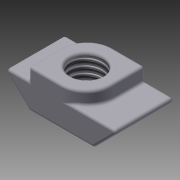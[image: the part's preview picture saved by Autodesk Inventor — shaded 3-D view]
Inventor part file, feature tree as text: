
AUTODESK INVENTOR PART (.ipt)
format: ipt  version: 2011 (Build 150239000, 239)  size: 196,608 bytes
history: native  units: in
note: dims shown in document units (in); Inventor stores cm internally (conversion verified against a paired STEP export)
features: extrude x2, fillet x2, sketch x2, thread x1
ambient origin geometry x8: Origin, YZ Plane, XZ Plane, XY Plane, X Axis, Y Axis, Z Axis, Center Point
bodies: Solid1 (feature_tree)
feature tree (7):
  extrude  "Extrusion1"  Depth=0.225in
  extrude  "Extrusion2"  Depth=0.25in
  fillet  "Fillet1"  Radius=0.1in
  fillet  "Fillet2"  Radius=0.05in
  thread  "Thread1"  [1 undecoded]
  sketch  "Sketch1"  dims[d0=0.45in d1=0.225in]
  sketch  "Sketch2"  dims[d2=0.1in d3=0.25in d4=0.1in d5=0.05in d6=0.1in d7=0.225in d8=0.0in d9=0.125in d10=1.0in d11=0.0in d12=0.1in d13=0.01in d14=1.0in d15=0.0in]
note: 1 required parameter value undecoded (feature->parameter linkage not recoverable at this tier; creation-order binding heuristic only, values carry confidence <= 0.55)
